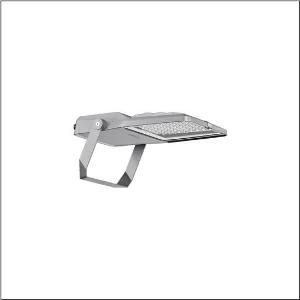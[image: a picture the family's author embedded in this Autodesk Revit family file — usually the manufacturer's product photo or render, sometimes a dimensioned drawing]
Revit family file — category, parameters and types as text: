
# Revit family: floodlight_fl_21_iq_mini___pl43_5xa7772d3a1a_c631
name_source: partatom
category: Lighting Fixtures
units: mm (PartAtom-declared; Revit-internal decimal feet)

## family parameters
Cut with Voids When Loaded = No
Host = Face
Light Source = No
Part Type = Normal
Room Calculation Point = No
Round Connector Dimension = Use Diameter
Shared = No

## types (1)
- --- (1 x LED, 15730 lm, 143 W, 3000K)
    Apparent Load = 143 VA
    CIE Flux Codes = 27 78 99 100 100
    Color Rendering = 80
    Color Temperature = 3000K
    Default Elevation = 1800 mm
    Description = Floodlight FL 21 iQ mini, floodlight, primary light control with lens, of PMMA, primary optical cover: protective disc, of toughened safety glass, transparent, light distribution: PL43, light emission: direct distribution, installation type: surface-mounted, lamps: LED, High Power LED, rated values: 15.730lm | 143W | 110lm/W (begin service life); end service life: 15.730lm | 151,6W; at 50% lumin. flux: 7.865lm | 60,5W | 130lm/W, colour temperature: 3000K, colour rendering: CRI > 80, light colour: 830, light setting 1 begin service life: 100% | 15.730lm | 143W | 110lm/W | 3.000K, light setting 1 end service life: 151,6W, further light settings possible, control: Street-Remote, Auto-Match, Temp-Guard, Night-Set, Smart-Wire, Desk-Remote (wireless, voltage-free reading and setting of iQ features in the workshop via application-optimized NFC function/RFID function), optimised constant luminous flux control (CLO 2.0), pre-setting: linear dimming characteristic, with terminal, 6-pole, mains connection: 220..240V, AC, 50/60Hz, luminaire housing, of diecast aluminium, powder-coated, SITECO metallic grey (DB 702S), corrosivity category C5 mid according to DIN EN ISO 12944suitable for swimming poolschlorine-resistant, sealing non-destructively replaceable, mounting bracket, of steel, galvanised, powder-coated, SITECO metallic grey (DB 702S), protection rating (complete): IP66, insulation class (complete): insulation class II (safety insulation), certification: CE, ENEC, VDE, protection symbol: D, impact resistance: IK08, permissible operating ambient temperature: -40..+40°C, permissible operating ambient temperature for outdoor applications: -40..+50°C, standard: DIN EN 12944, LABS conformity tested according to VDMA 24364:2018-05, packaging unit: 1 piece

Light Distribution: PL43
    Height = 70 mm
    Lamp = 1 x LED
    Lamp Light Flux = 15730 lm
    Lamp Power = 143 W
    Lamp count = 1
    Length = 485 mm
    Luminous efficacy = 110 lm/W
    Manufacturer = Siteco
    ModVariant = No
    Model = 5XA7772D3A1A
    Mounting Place = Pole
    Mounting Type = Pole annexe
    Number of Poles = 1
    OnlyDefault = Yes
    Power Factor = 1
    Product Name = Floodlight FL 21 iQ mini | PL43
    Product group = floodlight | pylon annexe
    ProductGroupID = 6201
    Protection Class = Protection class II
    Protection Degree = IP 66
    RLX_Detail_Level = 1
    RLX_Emergency_Light_Flux = 0 lm
    RLX_Emergency_Type = 0
    RLX_Emergency_Type_DB = No
    RlxData = <blob elided: 96657 chars, md5=9e6c7d7e>
    Socket = socket
    Standby Power = 0 W
    System Light Flux = 15730 lm
    System Power = 143 W
    Type Comments = factory setting: luminous flux: 100 % | dim-lin: 254 | 730 mA
    Type Image = l_1006845.jpg
    URL = http://relux.com
    VarID = @adj_162603
    Voltage = 0 V
    Weight = 0.00 kg
    Width = 337 mm

## geometry (parser evidence)
native form markers: Blend x4, Sweep x11
no freeform markers — native parametric forms only
